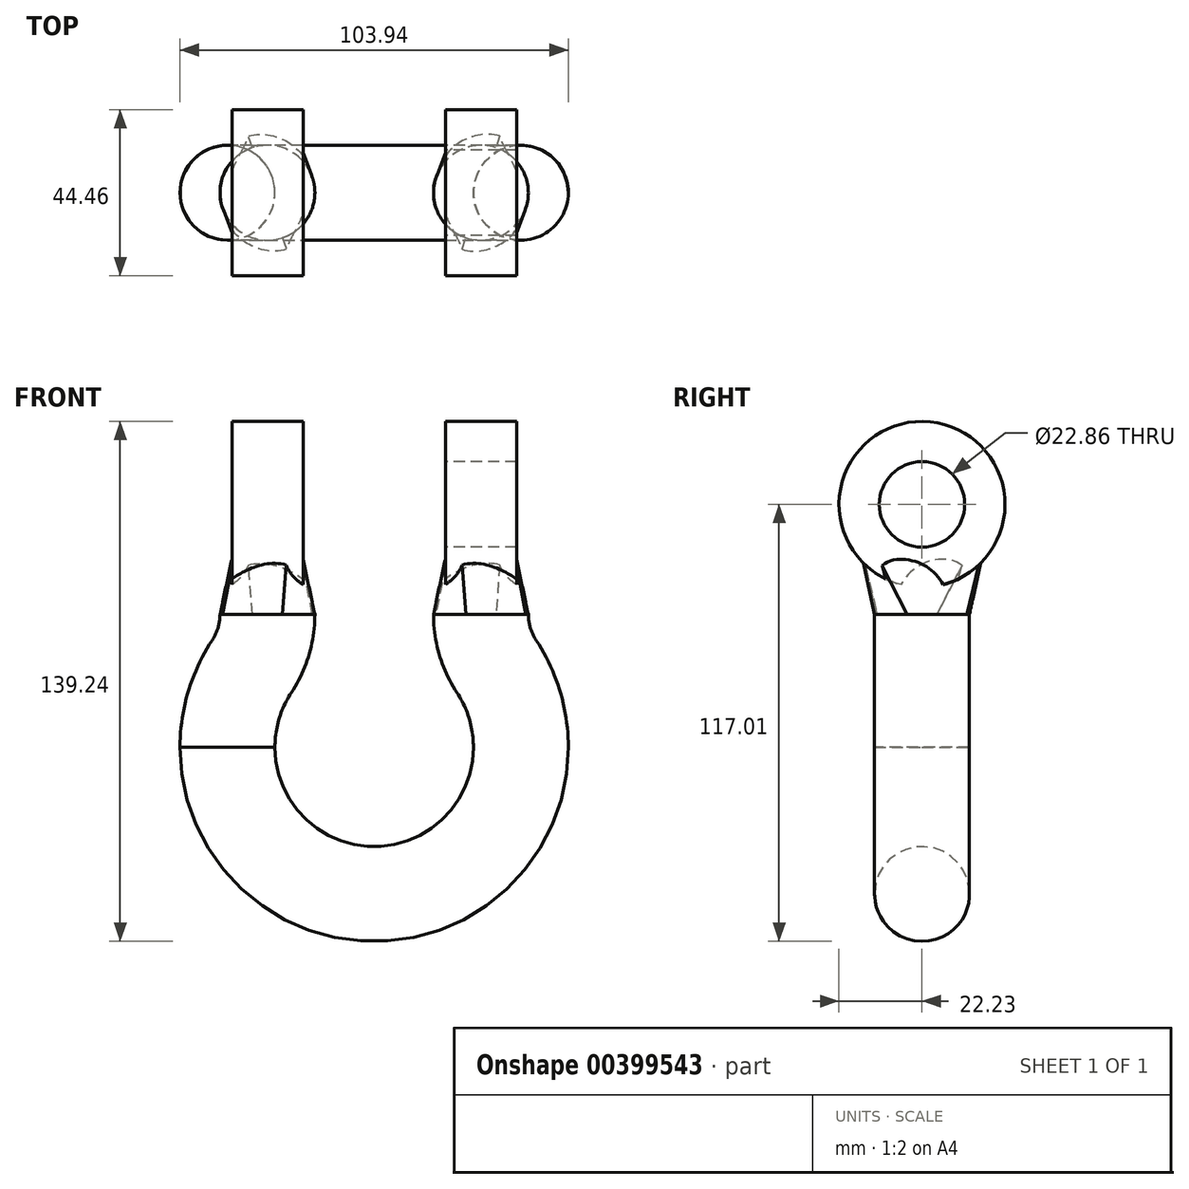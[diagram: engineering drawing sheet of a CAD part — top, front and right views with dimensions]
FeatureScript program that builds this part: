
annotation { "Feature Type Name" : "Feature", "Feature Type Description" : "" }
export const myFeature = defineFeature(function(context is Context, id is Id, definition is map)
    precondition{}
    {
        {
            var Q0;
            Q0=qCreatedBy(makeId("Right.planeOp"),FACE);
            cPlane(context, id + "F0", {"entities" : qUnion([Q0]), "cplaneType" : CPlaneType.OFFSET, "offset" : 19.05 * mm, "width" : 152.4 * mm, "height" : 152.4 * mm});
        }
        {
            var Q0;
            Q0=qCreatedBy(makeId("Right.planeOp"),FACE);
            cPlane(context, id + "F1", {"entities" : qUnion([Q0]), "cplaneType" : CPlaneType.OFFSET, "offset" : 19.05 * mm, "oppositeDirection" : true, "width" : 152.4 * mm, "height" : 152.4 * mm});
        }
        {
            var Q0;
            Q0=qCreatedBy(id+"F0.planeOp",FACE);
            var sketch = newSketch(context, id + "F2", { "sketchPlane" : qUnion([Q0])});
            skCircle(sketch, "E0", {"center": v(0, 0) * mm, "radius": 22.23 * mm});
            skCircle(sketch, "E1", {"center": v(0, 0) * mm, "radius": 12.7 * mm});
            skSolve(sketch);
        }
        {
            var Q0;
            Q0=qCreatedBy(id+"F1.planeOp",FACE);
            var sketch = newSketch(context, id + "F3", { "sketchPlane" : qUnion([Q0])});
            skCircle(sketch, "E2", {"center": v(0, 0) * mm, "radius": 22.23 * mm});
            skCircle(sketch, "E3", {"center": v(0, 0) * mm, "radius": 12.7 * mm});
            skSolve(sketch);
        }
        {
            var Q0;
            Q0=makeQuery(id+"F2.imprint","IMPRINT",FACE,{"disambiguationData":[TD([[makeQuery(id+"F2.imprint","IMPRINT",EDGE,{"derivedFrom":sQuery(id+"F2.wireOp",EDGE,"E0")}),1.0]])]});
            var Q1;
            Q1=makeQuery(id+"F2.imprint","IMPRINT",FACE,{"disambiguationData":[TD([[makeQuery(id+"F2.imprint","IMPRINT",EDGE,{"derivedFrom":sQuery(id+"F2.wireOp",EDGE,"E1")}),1.0]])]});
            extrude(context, id + "F4", {"entities" : qUnion([Q0, Q1]), "depth" : 19.05 * mm});
        }
        {
            var Q0;
            Q0=makeQuery(id+"F3.imprint","IMPRINT",FACE,{"disambiguationData":[TD([[makeQuery(id+"F3.imprint","IMPRINT",EDGE,{"derivedFrom":sQuery(id+"F3.wireOp",EDGE,"E2")}),1.0]])]});
            var Q1;
            Q1=makeQuery(id+"F3.imprint","IMPRINT",FACE,{"disambiguationData":[TD([[makeQuery(id+"F3.imprint","IMPRINT",EDGE,{"derivedFrom":sQuery(id+"F3.wireOp",EDGE,"E3")}),1.0]])]});
            extrude(context, id + "F5", {"entities" : qUnion([Q0, Q1]), "oppositeDirection" : true, "depth" : 19.05 * mm});
        }
        {
            var Q0;
            Q0=qCreatedBy(makeId("Front.planeOp"),FACE);
            var sketch = newSketch(context, id + "F6", { "sketchPlane" : qUnion([Q0])});
            skLineSegment(sketch, "E4", {"start": v(0, 0) * mm, "end": v(0, -76.2) * mm});
            skLineSegment(sketch, "E5", {"start": v(0, 0) * mm, "end": v(28.58, 0) * mm});
            skLineSegment(sketch, "E6", {"start": v(28.58, 0) * mm, "end": v(28.58, -29.41) * mm});
            skLineSegment(sketch, "E7", {"start": v(-38.1, 22.23) * mm, "end": v(-19.05, 22.23) * mm});
            skLineSegment(sketch, "E8", {"start": v(19.05, 22.23) * mm, "end": v(38.1, 22.23) * mm});
            skPoint(sketch, "E9", {"position": v(28.58, 22.23) * mm});
            skLineSegment(sketch, "E10.MirrorCS", {"start": v(0, 0) * mm, "end": v(-28.58, 0) * mm});
            skLineSegment(sketch, "E11.MirrorCS", {"start": v(-28.58, 0) * mm, "end": v(-28.58, -29.41) * mm});
            skArc(sketch, "E12", {"start": v(-32.78, -43.4) * mm, "mid": v(-37.61, -53.75) * mm, "end": v(-39.27, -65.04) * mm});
            skPoint(sketch, "E12.third.point", {"position": v(11.09, -102.71) * mm});
            skPoint(sketch, "E13.visualSharp", {"position": v(-28.58, -38.1) * mm});
            skArc(sketch, "E13.filletArc", {"start": v(-32.78, -43.4) * mm, "mid": v(-29.65, -36.72) * mm, "end": v(-28.58, -29.41) * mm});
            skPoint(sketch, "E14.visualSharp", {"position": v(28.58, -38.1) * mm});
            skArc(sketch, "E14.filletArc", {"start": v(28.58, -29.41) * mm, "mid": v(29.65, -36.72) * mm, "end": v(32.78, -43.4) * mm});
            skLineSegment(sketch, "E15", {"start": v(39.27, -65.04) * mm, "end": v(-39.27, -65.04) * mm});
            skArc(sketch, "E16", {"start": v(-39.27, -65.04) * mm, "mid": v(0, -104.31) * mm, "end": v(39.27, -65.04) * mm});
            skArc(sketch, "E17", {"start": v(39.27, -65.04) * mm, "mid": v(37.61, -53.75) * mm, "end": v(32.78, -43.4) * mm});
            skSolve(sketch);
        }
        {
            var Q0;
            Q0=qCreatedBy(makeId("Top.planeOp"),FACE);
            var sketch = newSketch(context, id + "F7", { "sketchPlane" : qUnion([Q0])});
            skLineSegment(sketch, "E18.0", {"start": v(0, 0) * mm, "end": v(28.58, 0) * mm});
            skLineSegment(sketch, "E18.1", {"start": v(0, 0) * mm, "end": v(-28.58, 0) * mm});
            skLineSegment(sketch, "E19.bottom", {"start": v(34.93, 19.05) * mm, "end": v(22.23, 19.05) * mm});
            skLineSegment(sketch, "E19.top", {"start": v(34.93, -19.05) * mm, "end": v(22.23, -19.05) * mm});
            skLineSegment(sketch, "E19.left", {"start": v(34.93, 19.05) * mm, "end": v(34.93, -19.05) * mm});
            skLineSegment(sketch, "E19.right", {"start": v(22.23, 19.05) * mm, "end": v(22.23, -19.05) * mm});
            skPoint(sketch, "E19.middle", {"position": v(28.58, 0) * mm});
            skLineSegment(sketch, "E20.bottom", {"start": v(-34.93, 19.05) * mm, "end": v(-22.23, 19.05) * mm});
            skLineSegment(sketch, "E20.top", {"start": v(-34.93, -19.05) * mm, "end": v(-22.23, -19.05) * mm});
            skLineSegment(sketch, "E20.left", {"start": v(-34.93, 19.05) * mm, "end": v(-34.93, -19.05) * mm});
            skLineSegment(sketch, "E20.right", {"start": v(-22.23, 19.05) * mm, "end": v(-22.23, -19.05) * mm});
            skPoint(sketch, "E20.middle", {"position": v(-28.58, 0) * mm});
            skSolve(sketch);
        }
        {
            var Q0;
            Q0=qCreatedBy(makeId("Top.planeOp"),FACE);
            cPlane(context, id + "F8", {"entities" : qUnion([Q0]), "cplaneType" : CPlaneType.OFFSET, "offset" : 65.04 * mm, "oppositeDirection" : true, "width" : 152.4 * mm, "height" : 152.4 * mm});
        }
        {
            var Q0;
            Q0=qCreatedBy(id+"F8.planeOp",FACE);
            var sketch = newSketch(context, id + "F9", { "sketchPlane" : qUnion([Q0])});
            skLineSegment(sketch, "E21.0", {"start": v(39.27, 0) * mm, "end": v(-39.27, 0) * mm});
            skCircle(sketch, "E22", {"center": v(39.27, 0) * mm, "radius": 12.7 * mm});
            skCircle(sketch, "E23", {"center": v(-39.27, 0) * mm, "radius": 12.7 * mm});
            skSolve(sketch);
        }
        {
            var Q0;
            Q0=makeQuery(id+"F9.imprint","IMPRINT",FACE,{"disambiguationData":[TD([[makeQuery(id+"F9.imprint","IMPRINT",EDGE,{"derivedFrom":sQuery(id+"F9.wireOp",EDGE,"E22")}),1.0]])]});
            var Q1;
            Q1=sQuery(id+"F6.wireOp",EDGE,"E16");
            sweep(context, id + "F10", {"profiles" : qUnion([Q0]), "path" : qUnion([Q1])});
        }
        {
            var Q0;
            Q0=makeQuery(id+"F9.imprint","IMPRINT",FACE,{"disambiguationData":[TD([[makeQuery(id+"F9.imprint","IMPRINT",EDGE,{"derivedFrom":sQuery(id+"F9.wireOp",EDGE,"E22")}),1.0]])]});
            var Q1;
            Q1=sQuery(id+"F6.wireOp",EDGE,"E17");
            var Q2;
            Q2=sQuery(id+"F6.wireOp",EDGE,"E14.filletArc");
            sweep(context, id + "F11", {"operationType" : NewBodyOperationType.ADD, "profiles" : qUnion([Q0]), "path" : qUnion([Q1, Q2])});
        }
        {
            var Q0;
            Q0=makeQuery(id+"F9.imprint","IMPRINT",FACE,{"disambiguationData":[TD([[makeQuery(id+"F9.imprint","IMPRINT",EDGE,{"derivedFrom":sQuery(id+"F9.wireOp",EDGE,"E23")}),1.0]])]});
            var Q1;
            Q1=sQuery(id+"F6.wireOp",EDGE,"E12");
            var Q2;
            Q2=sQuery(id+"F6.wireOp",EDGE,"E13.filletArc");
            sweep(context, id + "F12", {"operationType" : NewBodyOperationType.ADD, "profiles" : qUnion([Q0]), "path" : qUnion([Q1, Q2])});
        }
        {
            var Q1;
            Q1=makeQuery(id+"F12.opSweep","CAP_FACE",FACE,{"disambiguationData":[OSD([sQuery(id+"F6.wireOp",VERTEX,"E13.filletArc.end"),sQuery(id+"F9.wireOp",EDGE,"E23")])],"isStart":false});
            var Q2;
            {var subQ2=sQuery(id+"F7.wireOp",EDGE,"E20.bottom");Q2=makeQuery(id+"F7.imprint","IMPRINT",FACE,{"disambiguationData":[TD([[makeQuery(id+"F7.imprint","IMPRINT",EDGE,{"derivedFrom":subQ2}),-1.0]])]});}
            loft(context, id + "F13", {"operationType" : NewBodyOperationType.ADD, "sheetProfilesArray" : [{ "sheetProfileEntities" : qUnion([Q1]) }, { "sheetProfileEntities" : qUnion([Q2]) }]});
        }
        {
            var Q1;
            {var subQ1=sQuery(id+"F7.wireOp",EDGE,"E19.bottom");Q1=makeQuery(id+"F7.imprint","IMPRINT",FACE,{"disambiguationData":[TD([[makeQuery(id+"F7.imprint","IMPRINT",EDGE,{"derivedFrom":subQ1}),1.0]])]});}
            var Q2;
            Q2=makeQuery(id+"F11.opSweep","CAP_FACE",FACE,{"disambiguationData":[OSD([sQuery(id+"F6.wireOp",VERTEX,"E14.filletArc.start"),sQuery(id+"F9.wireOp",EDGE,"E22")])],"isStart":false});
            loft(context, id + "F14", {"operationType" : NewBodyOperationType.ADD, "sheetProfilesArray" : [{ "sheetProfileEntities" : qUnion([Q1]) }, { "sheetProfileEntities" : qUnion([Q2]) }]});
        }
        {
            var Q0;
            Q0=makeQuery(id+"F5.opExtrude","CAP_FACE",FACE,{"disambiguationData":[OSD([sQuery(id+"F3.wireOp",EDGE,"E2")])],"isStart":false});
            var sketch = newSketch(context, id + "F15", { "sketchPlane" : qUnion([Q0])});
            skPoint(sketch, "E24.0", {"position": v(0, 0) * mm});
            skSolve(sketch);
        }
        {
            var Q0;
            Q0=sQuery(id+"F15.wireOp",VERTEX,"E24.0");
            var Q1;
            Q1=makeQuery(id+"F4.opExtrude","SWEPT_BODY",BODY,{"disambiguationData":[OSD([sQuery(id+"F2.wireOp",EDGE,"E0")])]});
            hole(context, id + "F16", {"style" : HoleStyle.SIMPLE, "endStyle" : HoleEndStyle.THROUGH, "holeDiameter" : 22.86 * mm, "locations" : qUnion([Q0]), "scope" : qUnion([Q1]), "isTappedThrough" : true});
        }
    });
